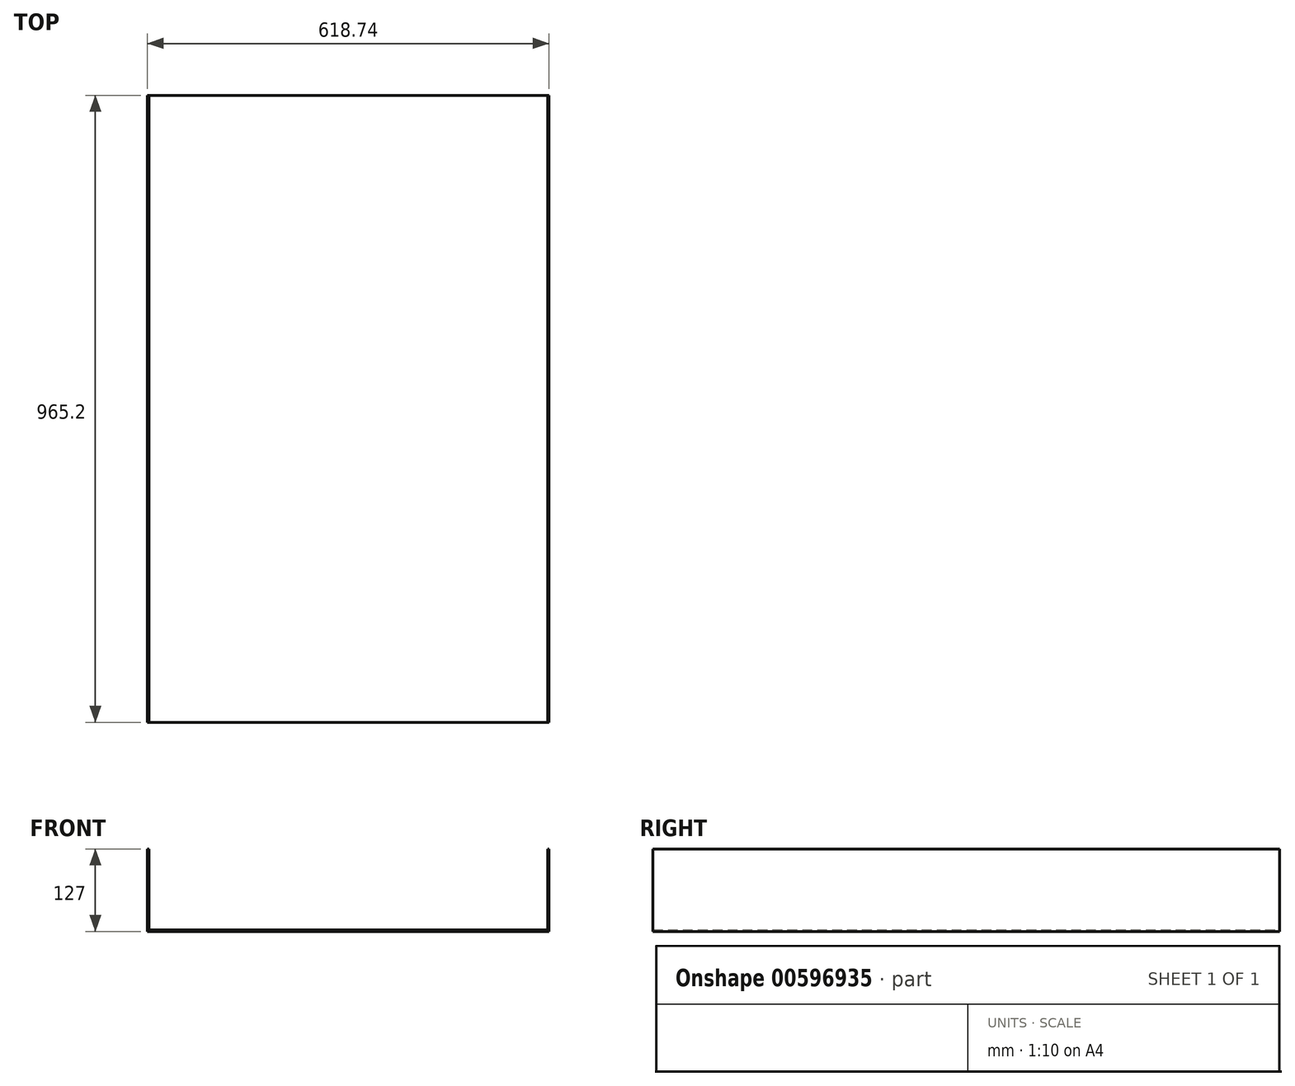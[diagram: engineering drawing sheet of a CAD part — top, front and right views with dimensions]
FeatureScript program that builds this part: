
annotation { "Feature Type Name" : "Feature", "Feature Type Description" : "" }
export const myFeature = defineFeature(function(context is Context, id is Id, definition is map)
    precondition{}
    {
        {
            var Q0;
            Q0=qCreatedBy(makeId("Front.planeOp"),FACE);
            var sketch = newSketch(context, id + "F0", { "sketchPlane" : qUnion([Q0])});
            skLineSegment(sketch, "E0", {"start": v(2.29, 127) * mm, "end": v(2.29, 2.29) * mm});
            skLineSegment(sketch, "E1", {"start": v(2.29, 2.29) * mm, "end": v(616.46, 2.29) * mm});
            skLineSegment(sketch, "E2", {"start": v(616.46, 2.29) * mm, "end": v(616.46, 127) * mm});
            skLineSegment(sketch, "E3.0", {"start": v(618.74, 0) * mm, "end": v(618.74, 127) * mm});
            skLineSegment(sketch, "E3.1", {"start": v(0, 0) * mm, "end": v(618.74, 0) * mm});
            skLineSegment(sketch, "E3.2", {"start": v(0, 127) * mm, "end": v(0, 0) * mm});
            skLineSegment(sketch, "E4", {"start": v(616.46, 127) * mm, "end": v(618.74, 127) * mm});
            skLineSegment(sketch, "E5", {"start": v(2.29, 127) * mm, "end": v(0, 127) * mm});
            skSolve(sketch);
        }
        {
            var Q0;
            Q0=makeQuery(id+"F0.imprint","IMPRINT",FACE,{"disambiguationData":[TD([[makeQuery(id+"F0.imprint","IMPRINT",EDGE,{"derivedFrom":sQuery(id+"F0.wireOp",EDGE,"E0")}),-1.0]])]});
            extrude(context, id + "F1", {"entities" : qUnion([Q0]), "depth" : 965.2 * mm, "offsetDistance" : 25.4 * mm});
        }
    });
